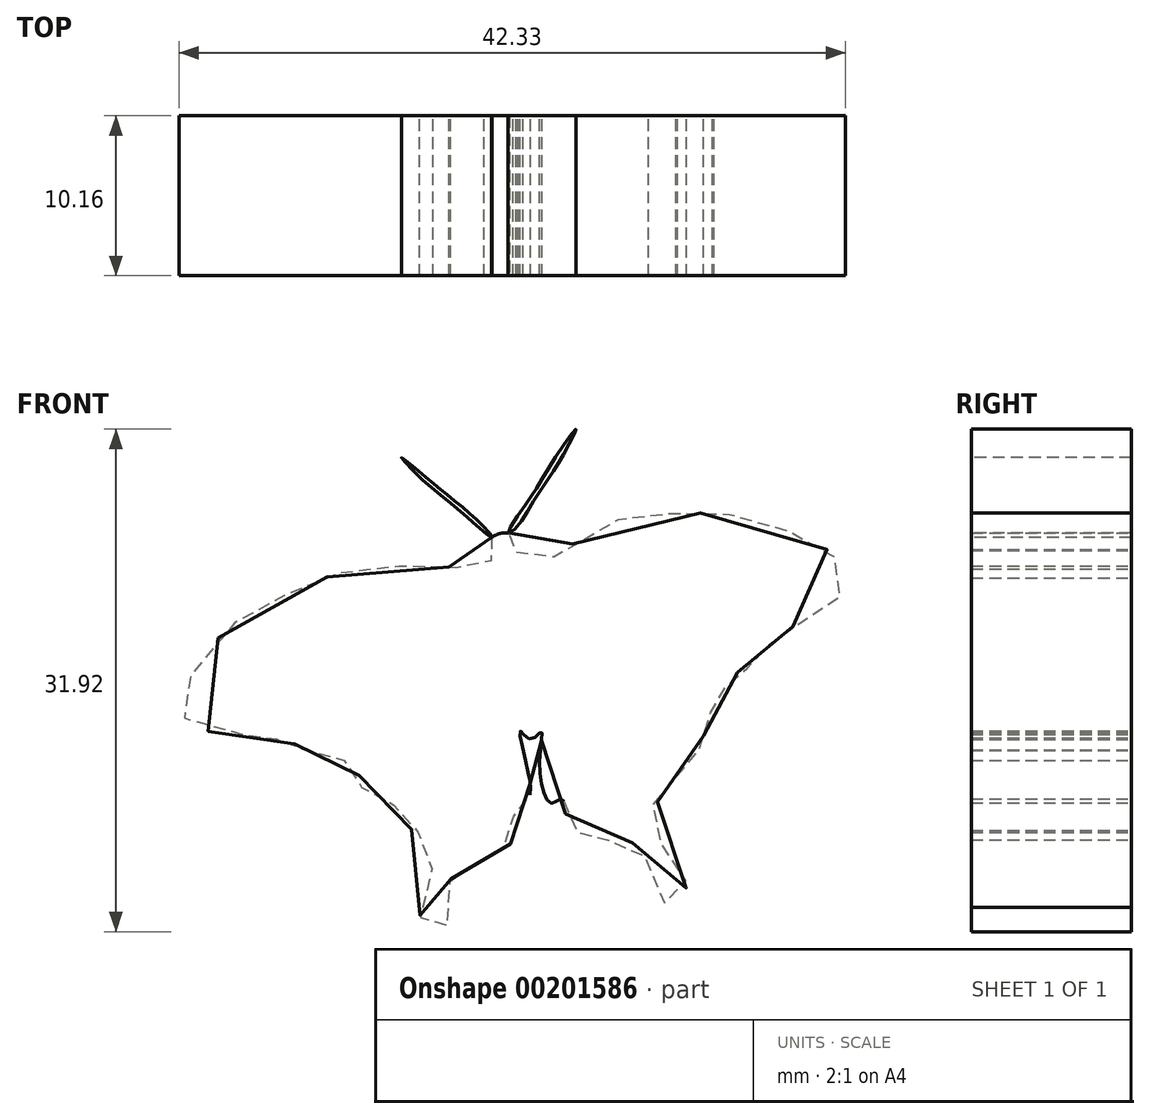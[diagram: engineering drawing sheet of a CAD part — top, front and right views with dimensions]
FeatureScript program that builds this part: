
annotation { "Feature Type Name" : "Feature", "Feature Type Description" : "" }
export const myFeature = defineFeature(function(context is Context, id is Id, definition is map)
    precondition{}
    {
        {
            var Q0;
            Q0=qCreatedBy(makeId("Front.planeOp"),FACE);
            var sketch = newSketch(context, id + "F0", { "sketchPlane" : qUnion([Q0])});
            skFitSpline(sketch, "E0", {"points": [v(-14.62, 2.82) * mm, v(-15.77, 3.19) * mm, v(-18.43, 3.5) * mm, v(-20.82, 3.45) * mm, v(-23.8, 3.03) * mm, v(-26.14, 2.2) * mm, v(-28.85, 0.79) * mm, v(-31.14, -0.72) * mm, v(-33.49, -3.9) * mm, v(-33.96, -5.36) * mm, v(-32.91, -6.72) * mm, v(-29.68, -7.19) * mm, v(-28.9, -7.19) * mm, v(-27.96, -7.5) * mm, v(-27.03, -7.45) * mm, v(-26.3, -8.12) * mm, v(-25.3, -8.23) * mm, v(-24.16, -8.8) * mm, v(-22.9, -8.9) * mm, v(-22.54, -9.69) * mm, v(-22.13, -10.83) * mm, v(-20.72, -11.2) * mm, v(-20.25, -11.88) * mm, v(-19.73, -12.87) * mm, v(-18.58, -13.5) * mm, v(-17.96, -14.07) * mm, v(-18.06, -16.46) * mm, v(-18.69, -18.34) * mm, v(-18.22, -19.49) * mm, v(-17.38, -19.7) * mm, v(-16.76, -18.86) * mm, v(-16.8, -17.09) * mm, v(-16.5, -15.94) * mm, v(-15.77, -15.37) * mm, v(-14.72, -15.21) * mm, v(-14.3, -14.54) * mm, v(-13.32, -14.38) * mm, v(-12.43, -13.39) * mm, v(-12.7, -12.5) * mm, v(-12.7, -12.19) * mm, v(-12.07, -12.03) * mm, v(-11.65, -10.89) * mm, v(-11.8, -9.53) * mm, v(-12.28, -6.98) * mm, v(-11.65, -7.5) * mm, v(-10.97, -7.03) * mm, v(-11.02, -8.28) * mm, v(-10.76, -11) * mm, v(-10.24, -11.56) * mm, v(-9.67, -11.3) * mm, v(-9.4, -12.24) * mm, v(-9.04, -13.39) * mm, v(-7.53, -13.34) * mm, v(-7.12, -13.8) * mm, v(-5.7, -13.9) * mm, v(-4.4, -14.9) * mm, v(-3.62, -17.2) * mm, v(-2.48, -18.18) * mm, v(-1.75, -16.67) * mm, v(-2.69, -14.85) * mm, v(-3.78, -13.44) * mm, v(-4.04, -11.88) * mm, v(-2.74, -11) * mm, v(-2.32, -9.84) * mm, v(-2.27, -8.9) * mm, v(-0.8, -8.07) * mm, v(-0.6, -6.46) * mm, v(0, -5.41) * mm, v(0, -4.48) * mm, v(1.22, -4.06) * mm, v(1.54, -3.22) * mm, v(2.42, -2.8) * mm, v(2.9, -1.71) * mm, v(3.93, -1.3) * mm, v(4.3, -0.67) * mm, v(6.07, 0) * mm, v(8.05, 1.62) * mm, v(8.31, 2.87) * mm, v(6.96, 4.75) * mm, v(4.46, 5.8) * mm, v(1.17, 6.73) * mm, v(-2.37, 6.83) * mm, v(-4.77, 6.63) * mm, v(-7.8, 5.74) * mm, v(-11.91, 3.34) * mm, v(-12.54, 4.44) * mm, v(-12.12, 4.85) * mm, v(-12.48, 5.43) * mm, v(-14.1, 5.32) * mm, v(-14.57, 4.49) * mm, v(-14.15, 4.54) * mm, v(-14.62, 2.82) * mm]});
            skFitSpline(sketch, "E1", {"points": [v(-14.1, 5.32) * mm, v(-16.5, 7.32) * mm, v(-18.7, 9.17) * mm, v(-19.83, 10.4) * mm, v(-18.2, 9.08) * mm, v(-17.03, 8.11) * mm, v(-15.71, 7.02) * mm, v(-14.57, 5.97) * mm, v(-14.1, 5.32) * mm]});
            skFitSpline(sketch, "E2", {"points": [v(-13.05, 5.6) * mm, v(-12.12, 7.15) * mm, v(-11.15, 8.6) * mm, v(-9.75, 10.87) * mm, v(-8.74, 12.19) * mm, v(-9.4, 10.87) * mm, v(-10.19, 9.52) * mm, v(-11.46, 7.59) * mm, v(-12.56, 5.92) * mm, v(-13.05, 5.6) * mm]});
            skSolve(sketch);
        }
        {
            var Q0;
            Q0 = qSketchRegion(id + "F0", true);
            extrude(context, id + "F1", {"entities" : qUnion([Q0]), "oppositeDirection" : true, "depth" : 10.16 * mm});
        }
    });
